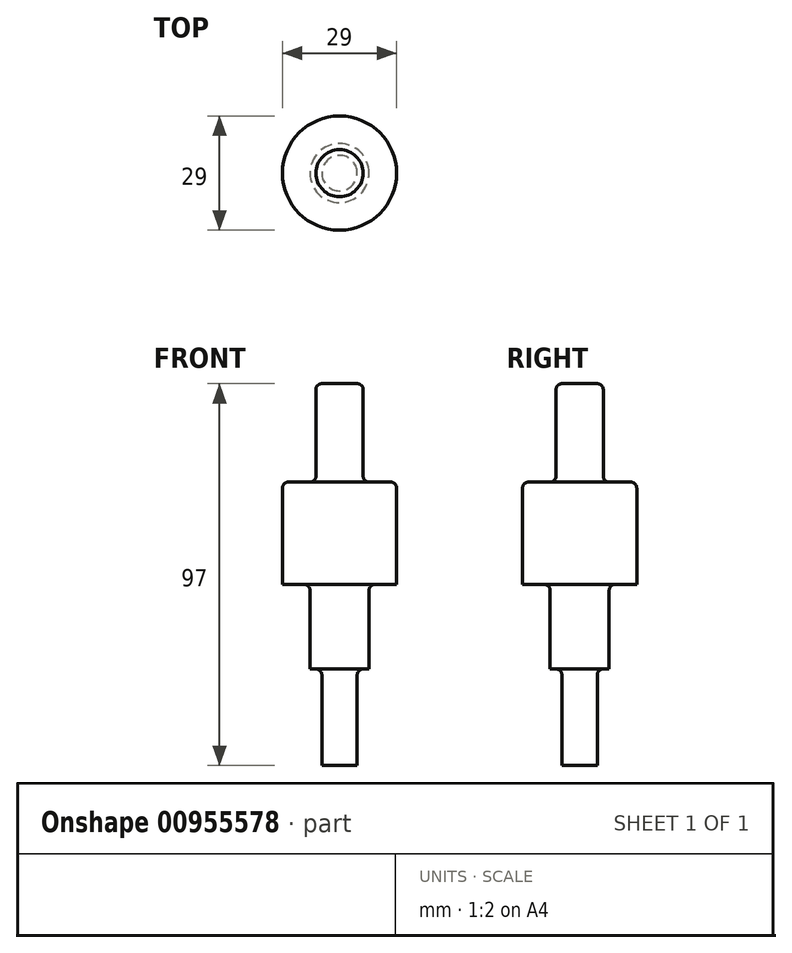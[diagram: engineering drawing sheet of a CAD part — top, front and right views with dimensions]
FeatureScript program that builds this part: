
annotation { "Feature Type Name" : "Feature", "Feature Type Description" : "" }
export const myFeature = defineFeature(function(context is Context, id is Id, definition is map)
    precondition{}
    {
        {
            var Q0;
            Q0=qCreatedBy(makeId("Front.planeOp"),FACE);
            var sketch = newSketch(context, id + "F0", { "sketchPlane" : qUnion([Q0])});
            skLineSegment(sketch, "E0", {"start": v(0, 0) * mm, "end": v(-4.5, 0) * mm});
            skLineSegment(sketch, "E1", {"start": v(-4.5, 0) * mm, "end": v(-4.5, 23) * mm});
            skLineSegment(sketch, "E2", {"start": v(-6, 24.5) * mm, "end": v(-7.5, 24.5) * mm});
            skLineSegment(sketch, "E3", {"start": v(-7.5, 24.5) * mm, "end": v(-7.5, 44.5) * mm});
            skLineSegment(sketch, "E4", {"start": v(-9, 46) * mm, "end": v(-14.5, 46) * mm});
            skLineSegment(sketch, "E5", {"start": v(-14.5, 46) * mm, "end": v(-14.5, 70.5) * mm});
            skLineSegment(sketch, "E6", {"start": v(-13, 72) * mm, "end": v(-7.5, 72) * mm});
            skLineSegment(sketch, "E7", {"start": v(-6, 73.5) * mm, "end": v(-6, 95.5) * mm});
            skLineSegment(sketch, "E8", {"start": v(-4.5, 97) * mm, "end": v(0, 97) * mm});
            skPoint(sketch, "E9.visualSharp", {"position": v(-4.5, 24.5) * mm});
            skArc(sketch, "E9.filletArc", {"start": v(-4.5, 23) * mm, "mid": v(-4.94, 24.06) * mm, "end": v(-6, 24.5) * mm});
            skPoint(sketch, "E10.visualSharp", {"position": v(-7.5, 46) * mm});
            skArc(sketch, "E10.filletArc", {"start": v(-7.5, 44.5) * mm, "mid": v(-7.94, 45.56) * mm, "end": v(-9, 46) * mm});
            skPoint(sketch, "E11.visualSharp", {"position": v(-6, 72) * mm});
            skArc(sketch, "E11.filletArc", {"start": v(-7.5, 72) * mm, "mid": v(-6.44, 72.44) * mm, "end": v(-6, 73.5) * mm});
            skPoint(sketch, "E12.visualSharp", {"position": v(-6, 97) * mm});
            skArc(sketch, "E12.filletArc", {"start": v(-4.5, 97) * mm, "mid": v(-5.56, 96.56) * mm, "end": v(-6, 95.5) * mm});
            skPoint(sketch, "E13.visualSharp", {"position": v(-14.5, 72) * mm});
            skArc(sketch, "E13.filletArc", {"start": v(-13, 72) * mm, "mid": v(-14.06, 71.56) * mm, "end": v(-14.5, 70.5) * mm});
            skLineSegment(sketch, "E14", {"start": v(0, 0) * mm, "end": v(0, 101.66) * mm, "construction": true});
            skLineSegment(sketch, "E15", {"start": v(0, 97) * mm, "end": v(0, 0) * mm});
            skSolve(sketch);
        }
        {
            var Q0;
            Q0 = qSketchRegion(id + "F0", true);
            var Q1;
            Q1=sQuery(id+"F0.wireOp",EDGE,"E14");
            revolve(context, id + "F1", {"surfaceOperationType" : NewSurfaceOperationType.NEW, "entities" : qUnion([Q0]), "axis" : qUnion([Q1]), "revolveType" : RevolveType.FULL});
        }
    });
